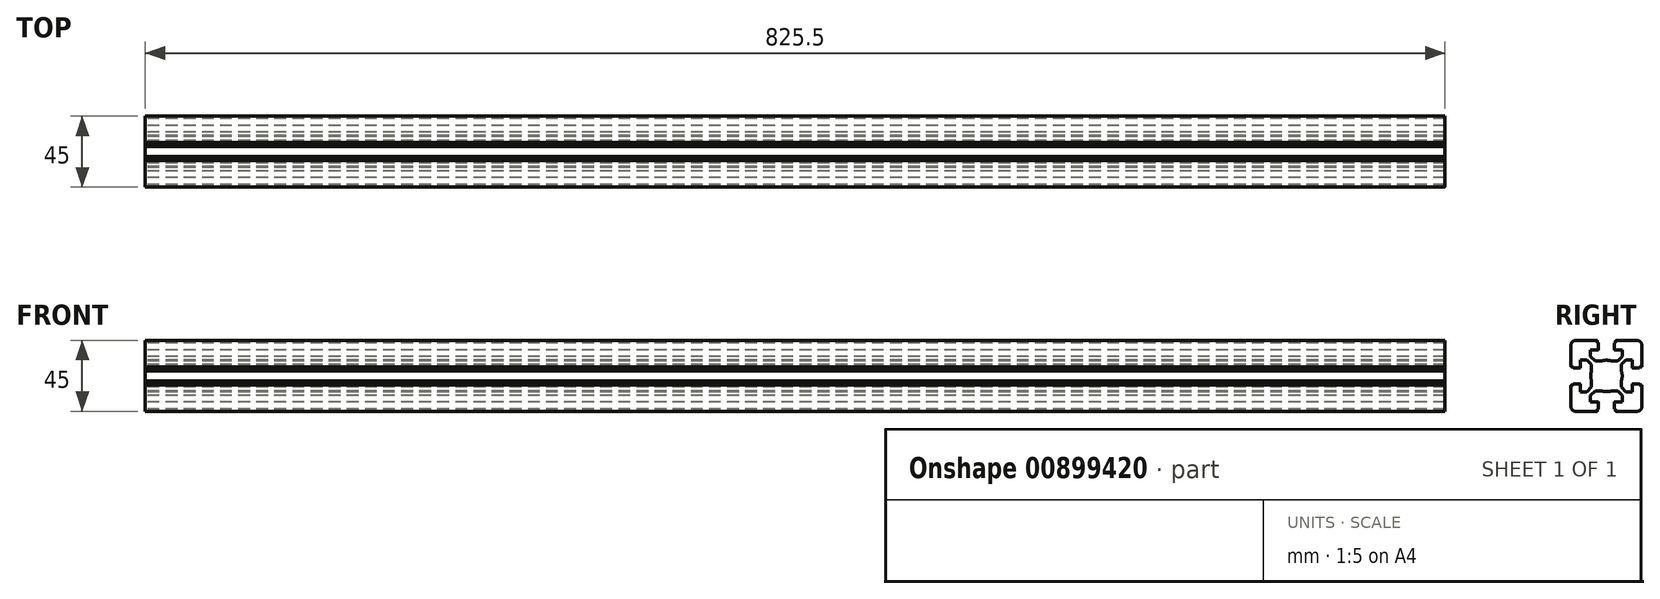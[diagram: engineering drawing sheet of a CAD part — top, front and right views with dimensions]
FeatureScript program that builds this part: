
annotation { "Feature Type Name" : "Feature", "Feature Type Description" : "" }
export const myFeature = defineFeature(function(context is Context, id is Id, definition is map)
    precondition{}
    {
        {
            var Q0;
            Q0=qCreatedBy(makeId("Right.planeOp"),FACE);
            var sketch = newSketch(context, id + "F0", { "sketchPlane" : qUnion([Q0])});
            skLineSegment(sketch, "E0", {"start": v(-20.09, -10.29) * mm, "end": v(-21.29, -10.29) * mm});
            skArc(sketch, "E1", {"start": v(-21.29, -10.29) * mm, "mid": v(-21.5, -10.38) * mm, "end": v(-21.59, -10.59) * mm});
            skLineSegment(sketch, "E2", {"start": v(-21.59, -10.59) * mm, "end": v(-21.59, -23.99) * mm});
            skArc(sketch, "E3", {"start": v(-21.59, -23.99) * mm, "mid": v(-20.7, -26.11) * mm, "end": v(-18.59, -26.99) * mm});
            skLineSegment(sketch, "E4", {"start": v(-18.59, -26.99) * mm, "end": v(-5.19, -26.99) * mm});
            skArc(sketch, "E5", {"start": v(-5.19, -26.99) * mm, "mid": v(-4.98, -26.9) * mm, "end": v(-4.89, -26.69) * mm});
            skLineSegment(sketch, "E6", {"start": v(-4.89, -26.69) * mm, "end": v(-4.89, -25.49) * mm});
            skLineSegment(sketch, "E7", {"start": v(-4.89, -25.49) * mm, "end": v(-4.39, -25.49) * mm});
            skArc(sketch, "E8", {"start": v(-4.39, -25.49) * mm, "mid": v(-4.18, -25.4) * mm, "end": v(-4.09, -25.19) * mm});
            skLineSegment(sketch, "E9", {"start": v(-4.09, -25.19) * mm, "end": v(-4.09, -21.29) * mm});
            skArc(sketch, "E10", {"start": v(-4.09, -21.29) * mm, "mid": v(-4.18, -21.08) * mm, "end": v(-4.39, -20.99) * mm});
            skLineSegment(sketch, "E11", {"start": v(-4.39, -20.99) * mm, "end": v(-9.14, -20.99) * mm});
            skLineSegment(sketch, "E12", {"start": v(-9.14, -20.99) * mm, "end": v(-9.14, -16.88) * mm});
            skLineSegment(sketch, "E13", {"start": v(-9.14, -16.88) * mm, "end": v(-6.25, -13.99) * mm});
            skLineSegment(sketch, "E14", {"start": v(-6.25, -13.99) * mm, "end": v(-2.21, -13.99) * mm});
            skArc(sketch, "E15", {"start": v(-2.21, -13.99) * mm, "mid": v(0.91, -14.49) * mm, "end": v(4.03, -13.99) * mm});
            skLineSegment(sketch, "E16", {"start": v(-20.09, -10.29) * mm, "end": v(-20.09, -9.79) * mm});
            skArc(sketch, "E17", {"start": v(-20.09, -9.79) * mm, "mid": v(-20, -9.58) * mm, "end": v(-19.79, -9.49) * mm});
            skLineSegment(sketch, "E18", {"start": v(-19.79, -9.49) * mm, "end": v(-15.89, -9.49) * mm});
            skArc(sketch, "E19", {"start": v(-15.89, -9.49) * mm, "mid": v(-15.68, -9.58) * mm, "end": v(-15.59, -9.79) * mm});
            skLineSegment(sketch, "E20", {"start": v(-15.59, -9.79) * mm, "end": v(-15.59, -14.54) * mm});
            skLineSegment(sketch, "E21", {"start": v(-15.59, -14.54) * mm, "end": v(-11.48, -14.54) * mm});
            skLineSegment(sketch, "E22", {"start": v(-11.48, -14.54) * mm, "end": v(-8.59, -11.65) * mm});
            skLineSegment(sketch, "E23", {"start": v(-8.59, -11.65) * mm, "end": v(-8.59, -7.61) * mm});
            skLineSegment(sketch, "E24", {"start": v(29.82, -4.49) * mm, "end": v(-31.05, -4.49) * mm});
            skLineSegment(sketch, "E25.MirrorCS", {"start": v(6.71, -25.49) * mm, "end": v(6.21, -25.49) * mm});
            skArc(sketch, "E26.MirrorCS", {"start": v(7.01, -26.99) * mm, "mid": v(6.8, -26.9) * mm, "end": v(6.71, -26.69) * mm});
            skLineSegment(sketch, "E27.MirrorCS", {"start": v(10.41, -11.65) * mm, "end": v(10.41, -7.61) * mm});
            skArc(sketch, "E28.MirrorCS", {"start": v(6.21, -25.49) * mm, "mid": v(6, -25.4) * mm, "end": v(5.91, -25.19) * mm});
            skLineSegment(sketch, "E29.MirrorCS", {"start": v(6.71, -26.69) * mm, "end": v(6.71, -25.49) * mm});
            skArc(sketch, "E30.MirrorCS", {"start": v(5.91, -21.29) * mm, "mid": v(6, -21.08) * mm, "end": v(6.21, -20.99) * mm});
            skLineSegment(sketch, "E31.MirrorCS", {"start": v(10.96, -16.88) * mm, "end": v(8.07, -13.99) * mm});
            skLineSegment(sketch, "E32.MirrorCS", {"start": v(13.3, -14.54) * mm, "end": v(10.41, -11.65) * mm});
            skLineSegment(sketch, "E33.MirrorCS", {"start": v(17.41, -14.54) * mm, "end": v(13.3, -14.54) * mm});
            skLineSegment(sketch, "E34.MirrorCS", {"start": v(17.41, -9.79) * mm, "end": v(17.41, -14.54) * mm});
            skLineSegment(sketch, "E35.MirrorCS", {"start": v(6.21, -20.99) * mm, "end": v(10.96, -20.99) * mm});
            skLineSegment(sketch, "E36.MirrorCS", {"start": v(8.07, -13.99) * mm, "end": v(4.03, -13.99) * mm});
            skArc(sketch, "E37.MirrorCS", {"start": v(4.03, -13.99) * mm, "mid": v(0.91, -14.49) * mm, "end": v(-2.21, -13.99) * mm});
            skLineSegment(sketch, "E38.MirrorCS", {"start": v(10.96, -20.99) * mm, "end": v(10.96, -16.88) * mm});
            skLineSegment(sketch, "E39.MirrorCS", {"start": v(5.91, -25.19) * mm, "end": v(5.91, -21.29) * mm});
            skArc(sketch, "E40.MirrorCS", {"start": v(23.41, -23.99) * mm, "mid": v(22.53, -26.11) * mm, "end": v(20.41, -26.99) * mm});
            skLineSegment(sketch, "E41.MirrorCS", {"start": v(20.41, -26.99) * mm, "end": v(7.01, -26.99) * mm});
            skLineSegment(sketch, "E42.MirrorCS", {"start": v(23.41, -10.59) * mm, "end": v(23.41, -23.99) * mm});
            skArc(sketch, "E43.MirrorCS", {"start": v(17.71, -9.49) * mm, "mid": v(17.5, -9.58) * mm, "end": v(17.41, -9.79) * mm});
            skArc(sketch, "E44.MirrorCS", {"start": v(23.11, -10.29) * mm, "mid": v(23.32, -10.38) * mm, "end": v(23.41, -10.59) * mm});
            skLineSegment(sketch, "E45.MirrorCS", {"start": v(21.91, -10.29) * mm, "end": v(21.91, -9.79) * mm});
            skLineSegment(sketch, "E46.MirrorCS", {"start": v(21.91, -10.29) * mm, "end": v(23.11, -10.29) * mm});
            skArc(sketch, "E47.MirrorCS", {"start": v(21.91, -9.79) * mm, "mid": v(21.82, -9.58) * mm, "end": v(21.61, -9.49) * mm});
            skLineSegment(sketch, "E48.MirrorCS", {"start": v(21.61, -9.49) * mm, "end": v(17.71, -9.49) * mm});
            skLineSegment(sketch, "E49.MirrorCS", {"start": v(6.71, 16.51) * mm, "end": v(6.21, 16.51) * mm});
            skArc(sketch, "E50.MirrorCS", {"start": v(-4.39, 16.51) * mm, "mid": v(-4.18, 16.42) * mm, "end": v(-4.09, 16.21) * mm});
            skLineSegment(sketch, "E51.MirrorCS", {"start": v(-4.89, 16.51) * mm, "end": v(-4.39, 16.51) * mm});
            skArc(sketch, "E52.MirrorCS", {"start": v(5.91, 12.31) * mm, "mid": v(6, 12.1) * mm, "end": v(6.21, 12.01) * mm});
            skLineSegment(sketch, "E53.MirrorCS", {"start": v(6.71, 17.71) * mm, "end": v(6.71, 16.51) * mm});
            skLineSegment(sketch, "E54.MirrorCS", {"start": v(-4.89, 17.71) * mm, "end": v(-4.89, 16.51) * mm});
            skArc(sketch, "E55.MirrorCS", {"start": v(-5.19, 18.01) * mm, "mid": v(-4.98, 17.92) * mm, "end": v(-4.89, 17.71) * mm});
            skArc(sketch, "E56.MirrorCS", {"start": v(-4.09, 12.31) * mm, "mid": v(-4.18, 12.1) * mm, "end": v(-4.39, 12.01) * mm});
            skArc(sketch, "E57.MirrorCS", {"start": v(7.01, 18.01) * mm, "mid": v(6.8, 17.92) * mm, "end": v(6.71, 17.71) * mm});
            skArc(sketch, "E58.MirrorCS", {"start": v(6.21, 16.51) * mm, "mid": v(6, 16.42) * mm, "end": v(5.91, 16.21) * mm});
            skArc(sketch, "E59.MirrorCS", {"start": v(23.11, 1.31) * mm, "mid": v(23.32, 1.4) * mm, "end": v(23.41, 1.61) * mm});
            skLineSegment(sketch, "E60.MirrorCS", {"start": v(21.91, 1.31) * mm, "end": v(21.91, 0.81) * mm});
            skArc(sketch, "E61.MirrorCS", {"start": v(-15.89, 0.51) * mm, "mid": v(-15.68, 0.6) * mm, "end": v(-15.59, 0.81) * mm});
            skArc(sketch, "E62.MirrorCS", {"start": v(-21.29, 1.31) * mm, "mid": v(-21.5, 1.4) * mm, "end": v(-21.59, 1.61) * mm});
            skArc(sketch, "E63.MirrorCS", {"start": v(17.71, 0.51) * mm, "mid": v(17.5, 0.6) * mm, "end": v(17.41, 0.81) * mm});
            skArc(sketch, "E64.MirrorCS", {"start": v(21.91, 0.81) * mm, "mid": v(21.82, 0.6) * mm, "end": v(21.61, 0.51) * mm});
            skLineSegment(sketch, "E65.MirrorCS", {"start": v(21.91, 1.31) * mm, "end": v(23.11, 1.31) * mm});
            skArc(sketch, "E66.MirrorCS", {"start": v(14.31, 5.31) * mm, "mid": v(14.1, 5.4) * mm, "end": v(14.01, 5.61) * mm});
            skArc(sketch, "E67.MirrorCS", {"start": v(-20.09, 0.81) * mm, "mid": v(-20, 0.6) * mm, "end": v(-19.79, 0.51) * mm});
            skLineSegment(sketch, "E68.MirrorCS", {"start": v(-20.09, 1.31) * mm, "end": v(-21.29, 1.31) * mm});
            skLineSegment(sketch, "E69.MirrorCS", {"start": v(-20.09, 1.31) * mm, "end": v(-20.09, 0.81) * mm});
            skLineSegment(sketch, "E70.MirrorCS", {"start": v(8.07, 5.01) * mm, "end": v(4.03, 5.01) * mm});
            skLineSegment(sketch, "E71.MirrorCS", {"start": v(-4.09, 16.21) * mm, "end": v(-4.09, 12.31) * mm});
            skLineSegment(sketch, "E72.MirrorCS", {"start": v(-9.14, 12.01) * mm, "end": v(-9.14, 7.9) * mm});
            skLineSegment(sketch, "E73.MirrorCS", {"start": v(-15.59, 5.56) * mm, "end": v(-11.48, 5.56) * mm});
            skLineSegment(sketch, "E74.MirrorCS", {"start": v(-4.39, 12.01) * mm, "end": v(-9.14, 12.01) * mm});
            skLineSegment(sketch, "E75.MirrorCS", {"start": v(-9.14, 7.9) * mm, "end": v(-6.25, 5.01) * mm});
            skLineSegment(sketch, "E76.MirrorCS", {"start": v(10.96, 12.01) * mm, "end": v(10.96, 7.9) * mm});
            skArc(sketch, "E77.MirrorCS", {"start": v(-21.59, 15.01) * mm, "mid": v(-20.7, 17.13) * mm, "end": v(-18.59, 18.01) * mm});
            skLineSegment(sketch, "E78.MirrorCS", {"start": v(23.41, 1.61) * mm, "end": v(23.41, 15.01) * mm});
            skLineSegment(sketch, "E79.MirrorCS", {"start": v(13.3, 5.56) * mm, "end": v(10.41, 2.67) * mm});
            skLineSegment(sketch, "E80.MirrorCS", {"start": v(-8.59, 2.67) * mm, "end": v(-8.59, -1.37) * mm});
            skLineSegment(sketch, "E81.MirrorCS", {"start": v(-15.59, 0.81) * mm, "end": v(-15.59, 5.56) * mm});
            skLineSegment(sketch, "E82.MirrorCS", {"start": v(10.41, 2.67) * mm, "end": v(10.41, -1.37) * mm});
            skLineSegment(sketch, "E83.MirrorCS", {"start": v(-18.59, 18.01) * mm, "end": v(-5.19, 18.01) * mm});
            skLineSegment(sketch, "E84.MirrorCS", {"start": v(10.96, 7.9) * mm, "end": v(8.07, 5.01) * mm});
            skLineSegment(sketch, "E85.MirrorCS", {"start": v(17.41, 5.56) * mm, "end": v(13.3, 5.56) * mm});
            skArc(sketch, "E86.MirrorCS", {"start": v(23.41, 15.01) * mm, "mid": v(22.53, 17.13) * mm, "end": v(20.41, 18.01) * mm});
            skLineSegment(sketch, "E87.MirrorCS", {"start": v(5.91, 16.21) * mm, "end": v(5.91, 12.31) * mm});
            skLineSegment(sketch, "E88.MirrorCS", {"start": v(17.41, 0.81) * mm, "end": v(17.41, 5.56) * mm});
            skLineSegment(sketch, "E89.MirrorCS", {"start": v(-11.48, 5.56) * mm, "end": v(-8.59, 2.67) * mm});
            skLineSegment(sketch, "E90.MirrorCS", {"start": v(-6.25, 5.01) * mm, "end": v(-2.21, 5.01) * mm});
            skLineSegment(sketch, "E91.MirrorCS", {"start": v(-21.59, 1.61) * mm, "end": v(-21.59, 15.01) * mm});
            skArc(sketch, "E92.MirrorCS", {"start": v(4.03, 5.01) * mm, "mid": v(0.91, 5.51) * mm, "end": v(-2.21, 5.01) * mm});
            skLineSegment(sketch, "E93.MirrorCS", {"start": v(6.21, 12.01) * mm, "end": v(10.96, 12.01) * mm});
            skArc(sketch, "E94.MirrorCS", {"start": v(-2.21, 5.01) * mm, "mid": v(0.91, 5.51) * mm, "end": v(4.03, 5.01) * mm});
            skLineSegment(sketch, "E95.MirrorCS", {"start": v(20.41, 18.01) * mm, "end": v(7.01, 18.01) * mm});
            skLineSegment(sketch, "E96.MirrorCS", {"start": v(-19.79, 0.51) * mm, "end": v(-15.89, 0.51) * mm});
            skLineSegment(sketch, "E97.MirrorCS", {"start": v(21.61, 0.51) * mm, "end": v(17.71, 0.51) * mm});
            skLineSegment(sketch, "E98.MirrorCS", {"start": v(0.91, -27.65) * mm, "end": v(0.91, 19.82) * mm});
            skArc(sketch, "E99", {"start": v(-8.59, -1.37) * mm, "mid": v(-9.09, -4.49) * mm, "end": v(-8.59, -7.61) * mm});
            skArc(sketch, "E100", {"start": v(10.41, -7.61) * mm, "mid": v(10.91, -4.49) * mm, "end": v(10.41, -1.37) * mm});
            skSolve(sketch);
        }
        {
            var Q0;
            Q0=qSketchRegion(id+"F0",true);
            extrude(context, id + "F1", {"entities" : qUnion([Q0]), "depth" : 825.5 * mm, "offsetDistance" : 25.4 * mm});
        }
    });
